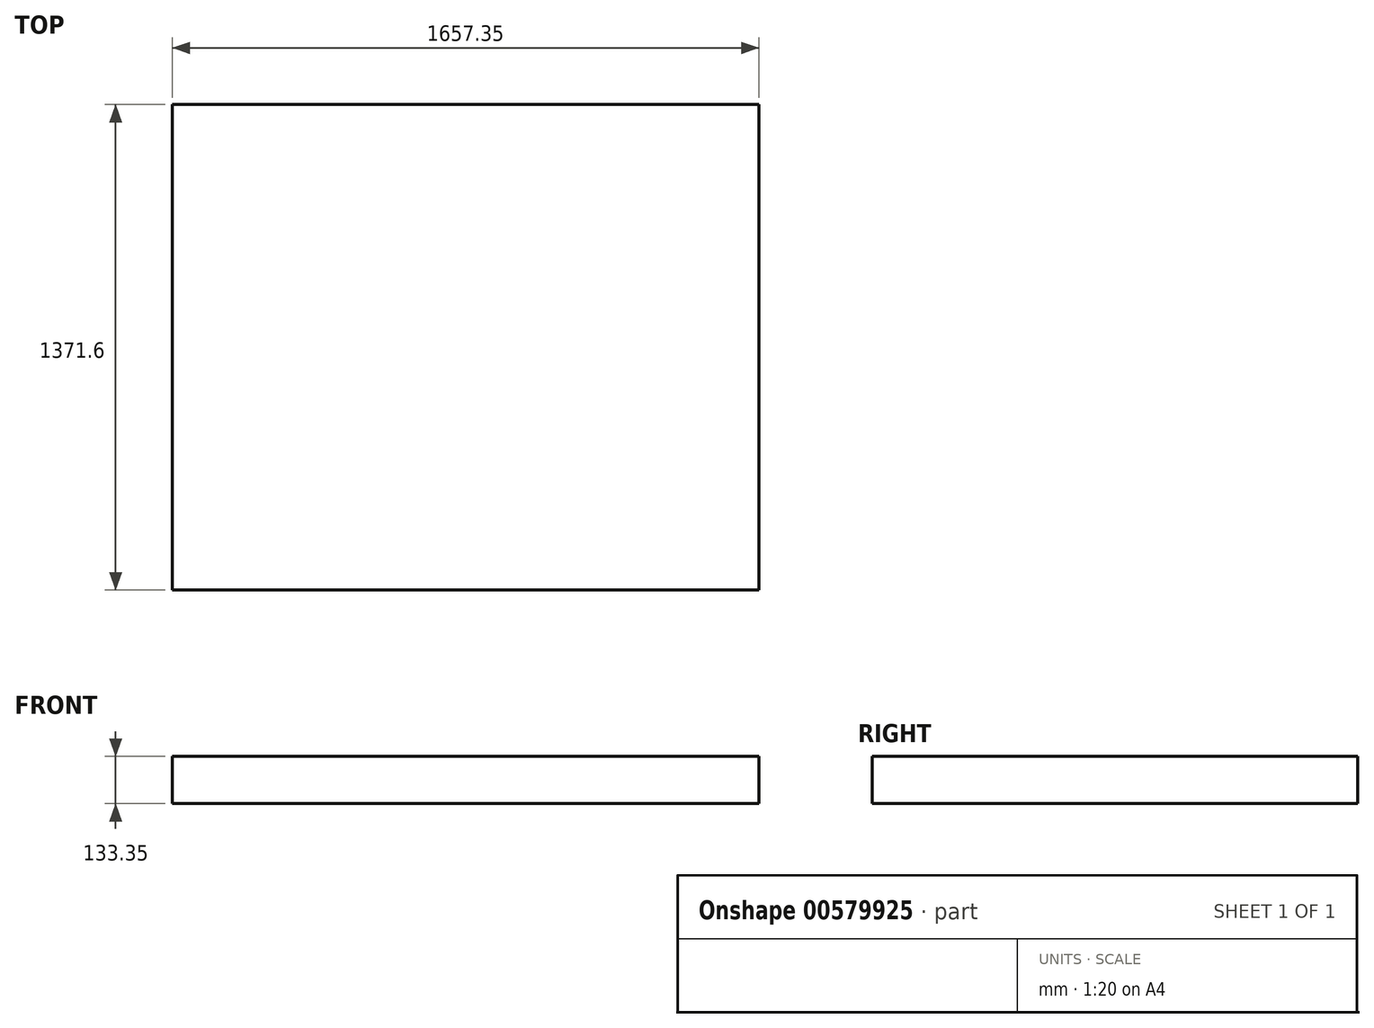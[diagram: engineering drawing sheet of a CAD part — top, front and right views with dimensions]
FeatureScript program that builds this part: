
annotation { "Feature Type Name" : "Feature", "Feature Type Description" : "" }
export const myFeature = defineFeature(function(context is Context, id is Id, definition is map)
    precondition{}
    {
        {
            var Q0;
            Q0=qCreatedBy(makeId("Top.planeOp"),FACE);
            var sketch = newSketch(context, id + "F0", { "sketchPlane" : qUnion([Q0])});
            skLineSegment(sketch, "E0.bottom", {"start": v(-817.93, 809.08) * mm, "end": v(839.42, 809.08) * mm});
            skLineSegment(sketch, "E0.top", {"start": v(-817.93, -562.52) * mm, "end": v(839.42, -562.52) * mm});
            skLineSegment(sketch, "E0.left", {"start": v(-817.93, 809.08) * mm, "end": v(-817.93, -562.52) * mm});
            skLineSegment(sketch, "E0.right", {"start": v(839.42, 809.08) * mm, "end": v(839.42, -562.52) * mm});
            skSolve(sketch);
        }
        {
            var Q0;
            Q0 = qSketchRegion(id + "F0", true);
            extrude(context, id + "F1", {"entities" : qUnion([Q0]), "depth" : 133.35 * mm, "offsetDistance" : 25.4 * mm});
        }
    });
